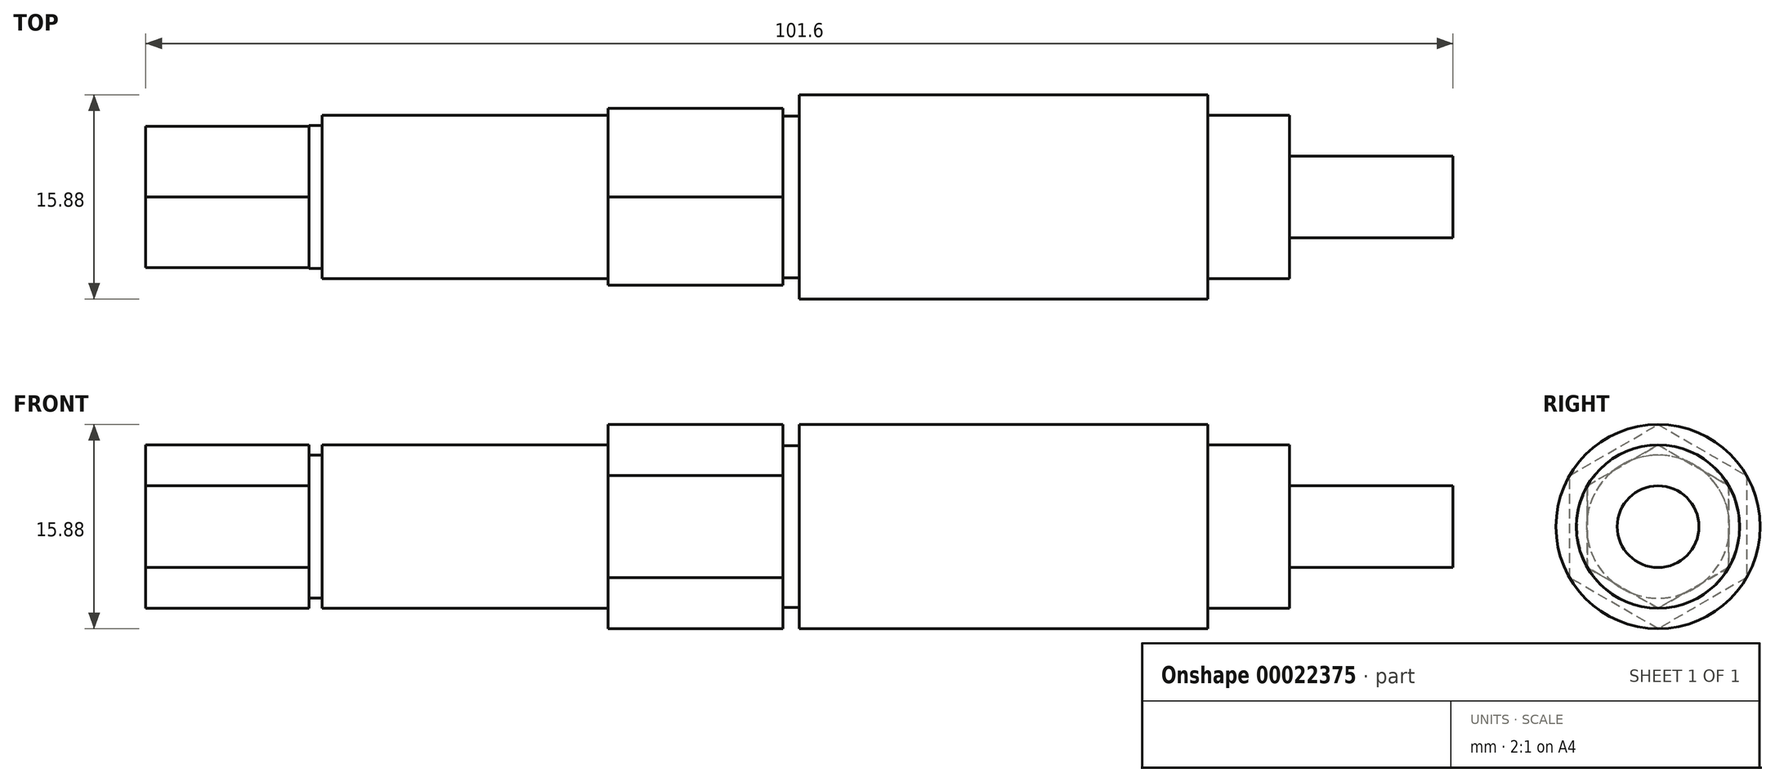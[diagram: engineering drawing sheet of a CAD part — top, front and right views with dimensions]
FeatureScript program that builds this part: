
annotation { "Feature Type Name" : "Feature", "Feature Type Description" : "" }
export const myFeature = defineFeature(function(context is Context, id is Id, definition is map)
    precondition{}
    {
        {
            var Q0;
            Q0=qCreatedBy(makeId("Front.planeOp"),FACE);
            var sketch = newSketch(context, id + "F0", { "sketchPlane" : qUnion([Q0])});
            skLineSegment(sketch, "E0", {"start": v(0, 0) * mm, "end": v(101.6, 0) * mm});
            skLineSegment(sketch, "E1", {"start": v(101.6, 0) * mm, "end": v(101.6, 3.18) * mm});
            skLineSegment(sketch, "E2", {"start": v(101.6, 3.18) * mm, "end": v(88.9, 3.18) * mm});
            skLineSegment(sketch, "E3", {"start": v(88.9, 3.18) * mm, "end": v(88.9, 6.35) * mm});
            skLineSegment(sketch, "E4", {"start": v(88.9, 6.35) * mm, "end": v(82.55, 6.35) * mm});
            skLineSegment(sketch, "E5", {"start": v(82.55, 6.35) * mm, "end": v(82.55, 7.94) * mm});
            skLineSegment(sketch, "E6", {"start": v(82.55, 7.94) * mm, "end": v(50.8, 7.94) * mm});
            skLineSegment(sketch, "E7", {"start": v(50.8, 7.94) * mm, "end": v(50.8, 6.29) * mm});
            skLineSegment(sketch, "E8", {"start": v(50.8, 6.29) * mm, "end": v(49.53, 6.29) * mm});
            skLineSegment(sketch, "E9", {"start": v(49.53, 6.29) * mm, "end": v(49.53, 7.94) * mm});
            skLineSegment(sketch, "E10", {"start": v(49.53, 7.94) * mm, "end": v(35.94, 7.94) * mm});
            skLineSegment(sketch, "E11", {"start": v(35.94, 7.94) * mm, "end": v(35.94, 6.35) * mm});
            skLineSegment(sketch, "E12", {"start": v(35.94, 6.35) * mm, "end": v(13.72, 6.35) * mm});
            skLineSegment(sketch, "E13", {"start": v(13.72, 6.35) * mm, "end": v(13.72, 5.56) * mm});
            skLineSegment(sketch, "E14", {"start": v(13.72, 5.56) * mm, "end": v(12.7, 5.56) * mm});
            skLineSegment(sketch, "E15", {"start": v(12.7, 5.56) * mm, "end": v(12.7, 6.35) * mm});
            skLineSegment(sketch, "E16", {"start": v(12.7, 6.35) * mm, "end": v(0, 6.35) * mm});
            skLineSegment(sketch, "E17", {"start": v(0, 6.35) * mm, "end": v(0, 0) * mm});
            skLineSegment(sketch, "E18", {"start": v(0, 0) * mm, "end": v(-14.7, 0) * mm, "construction": true});
            skSolve(sketch);
        }
        {
            var Q0;
            Q0=makeQuery(id+"F0.imprint","IMPRINT",FACE,{"disambiguationData":[TD([[makeQuery(id+"F0.imprint","IMPRINT",EDGE,{"derivedFrom":sQuery(id+"F0.wireOp",EDGE,"E0")}),1.0]])]});
            var Q1;
            Q1=sQuery(id+"F0.wireOp",EDGE,"E0");
            revolve(context, id + "F1", {"entities" : qUnion([Q0]), "axis" : qUnion([Q1]), "revolveType" : RevolveType.FULL});
        }
        {
            var Q0;
            Q0=makeQuery(id+"F1.opRevolve","SWEPT_FACE",FACE,{"disambiguationData":[OSD([sQuery(id+"F0.wireOp",EDGE,"E17")])]});
            var sketch = newSketch(context, id + "F2", { "sketchPlane" : qUnion([Q0])});
            skCircle(sketch, "E19.cCircle", {"center": v(0, 0) * mm, "radius": 6.35 * mm, "construction": true});
            skLineSegment(sketch, "E19.0", {"start": v(0, 6.35) * mm, "end": v(5.5, 3.18) * mm});
            skLineSegment(sketch, "E19.1", {"start": v(5.5, 3.18) * mm, "end": v(5.5, -3.17) * mm});
            skLineSegment(sketch, "E19.2", {"start": v(5.5, -3.17) * mm, "end": v(0, -6.35) * mm});
            skLineSegment(sketch, "E19.3", {"start": v(0, -6.35) * mm, "end": v(-5.5, -3.18) * mm});
            skLineSegment(sketch, "E19.4", {"start": v(-5.5, -3.18) * mm, "end": v(-5.5, 3.17) * mm});
            skLineSegment(sketch, "E19.5", {"start": v(-5.5, 3.17) * mm, "end": v(0, 6.35) * mm});
            skSolve(sketch);
        }
        {
            var Q0;
            {var subQ1=sQuery(id+"F2.wireOp",EDGE,"E19.0");Q0=makeQuery(id+"F2.imprint","IMPRINT",FACE,{"disambiguationData":[TD([[makeQuery(id+"F2.imprint","IMPRINT",EDGE,{"derivedFrom":subQ1}),1.0]])]});}
            var Q1;
            {var subQ1=sQuery(id+"F2.wireOp",EDGE,"E19.1");Q1=makeQuery(id+"F2.imprint","IMPRINT",FACE,{"disambiguationData":[TD([[makeQuery(id+"F2.imprint","IMPRINT",EDGE,{"derivedFrom":subQ1}),1.0]])]});}
            var Q2;
            {var subQ1=sQuery(id+"F2.wireOp",EDGE,"E19.2");Q2=makeQuery(id+"F2.imprint","IMPRINT",FACE,{"disambiguationData":[TD([[makeQuery(id+"F2.imprint","IMPRINT",EDGE,{"derivedFrom":subQ1}),1.0]])]});}
            var Q3;
            {var subQ1=sQuery(id+"F2.wireOp",EDGE,"E19.3");Q3=makeQuery(id+"F2.imprint","IMPRINT",FACE,{"disambiguationData":[TD([[makeQuery(id+"F2.imprint","IMPRINT",EDGE,{"derivedFrom":subQ1}),1.0]])]});}
            var Q4;
            {var subQ1=sQuery(id+"F2.wireOp",EDGE,"E19.4");Q4=makeQuery(id+"F2.imprint","IMPRINT",FACE,{"disambiguationData":[TD([[makeQuery(id+"F2.imprint","IMPRINT",EDGE,{"derivedFrom":subQ1}),1.0]])]});}
            var Q5;
            {var subQ1=sQuery(id+"F2.wireOp",EDGE,"E19.5");Q5=makeQuery(id+"F2.imprint","IMPRINT",FACE,{"disambiguationData":[TD([[makeQuery(id+"F2.imprint","IMPRINT",EDGE,{"derivedFrom":subQ1}),1.0]])]});}
            var Q6;
            Q6=makeQuery(id+"F1.opRevolve","SWEPT_FACE",FACE,{"disambiguationData":[OSD([sQuery(id+"F0.wireOp",EDGE,"E15")])]});
            extrude(context, id + "F3", {"entities" : qUnion([Q0, Q1, Q2, Q3, Q4, Q5]), "operationType" : NewBodyOperationType.REMOVE, "endBound" : BoundingType.UP_TO_SURFACE, "oppositeDirection" : true, "endBoundEntityFace" : qUnion([Q6]), "depth" : 25.4 * mm});
        }
        {
            var Q0;
            Q0=makeQuery(id+"F1.opRevolve","SWEPT_FACE",FACE,{"disambiguationData":[OSD([sQuery(id+"F0.wireOp",EDGE,"E11")])]});
            var sketch = newSketch(context, id + "F4", { "sketchPlane" : qUnion([Q0])});
            skCircle(sketch, "E20.cCircle", {"center": v(0, 0) * mm, "radius": 7.94 * mm, "construction": true});
            skLineSegment(sketch, "E20.0", {"start": v(0, 7.94) * mm, "end": v(6.87, 3.97) * mm});
            skLineSegment(sketch, "E20.1", {"start": v(6.87, 3.97) * mm, "end": v(6.87, -3.97) * mm});
            skLineSegment(sketch, "E20.2", {"start": v(6.87, -3.97) * mm, "end": v(0, -7.94) * mm});
            skLineSegment(sketch, "E20.3", {"start": v(0, -7.94) * mm, "end": v(-6.87, -3.97) * mm});
            skLineSegment(sketch, "E20.4", {"start": v(-6.87, -3.97) * mm, "end": v(-6.87, 3.97) * mm});
            skLineSegment(sketch, "E20.5", {"start": v(-6.87, 3.97) * mm, "end": v(0, 7.94) * mm});
            skSolve(sketch);
        }
        {
            var Q0;
            {var subQ1=sQuery(id+"F4.wireOp",EDGE,"E20.5");Q0=makeQuery(id+"F4.imprint","IMPRINT",FACE,{"disambiguationData":[TD([[makeQuery(id+"F4.imprint","IMPRINT",EDGE,{"derivedFrom":subQ1}),1.0]])]});}
            var Q1;
            {var subQ1=sQuery(id+"F4.wireOp",EDGE,"E20.0");Q1=makeQuery(id+"F4.imprint","IMPRINT",FACE,{"disambiguationData":[TD([[makeQuery(id+"F4.imprint","IMPRINT",EDGE,{"derivedFrom":subQ1}),1.0]])]});}
            var Q2;
            {var subQ1=sQuery(id+"F4.wireOp",EDGE,"E20.1");Q2=makeQuery(id+"F4.imprint","IMPRINT",FACE,{"disambiguationData":[TD([[makeQuery(id+"F4.imprint","IMPRINT",EDGE,{"derivedFrom":subQ1}),1.0]])]});}
            var Q3;
            {var subQ1=sQuery(id+"F4.wireOp",EDGE,"E20.2");Q3=makeQuery(id+"F4.imprint","IMPRINT",FACE,{"disambiguationData":[TD([[makeQuery(id+"F4.imprint","IMPRINT",EDGE,{"derivedFrom":subQ1}),1.0]])]});}
            var Q4;
            {var subQ1=sQuery(id+"F4.wireOp",EDGE,"E20.3");Q4=makeQuery(id+"F4.imprint","IMPRINT",FACE,{"disambiguationData":[TD([[makeQuery(id+"F4.imprint","IMPRINT",EDGE,{"derivedFrom":subQ1}),1.0]])]});}
            var Q5;
            {var subQ1=sQuery(id+"F4.wireOp",EDGE,"E20.4");Q5=makeQuery(id+"F4.imprint","IMPRINT",FACE,{"disambiguationData":[TD([[makeQuery(id+"F4.imprint","IMPRINT",EDGE,{"derivedFrom":subQ1}),1.0]])]});}
            var Q6;
            Q6=makeQuery(id+"F1.opRevolve","SWEPT_FACE",FACE,{"disambiguationData":[OSD([sQuery(id+"F0.wireOp",EDGE,"E9")])]});
            extrude(context, id + "F5", {"entities" : qUnion([Q0, Q1, Q2, Q3, Q4, Q5]), "operationType" : NewBodyOperationType.REMOVE, "endBound" : BoundingType.UP_TO_SURFACE, "oppositeDirection" : true, "endBoundEntityFace" : qUnion([Q6]), "depth" : 25.4 * mm});
        }
    });
